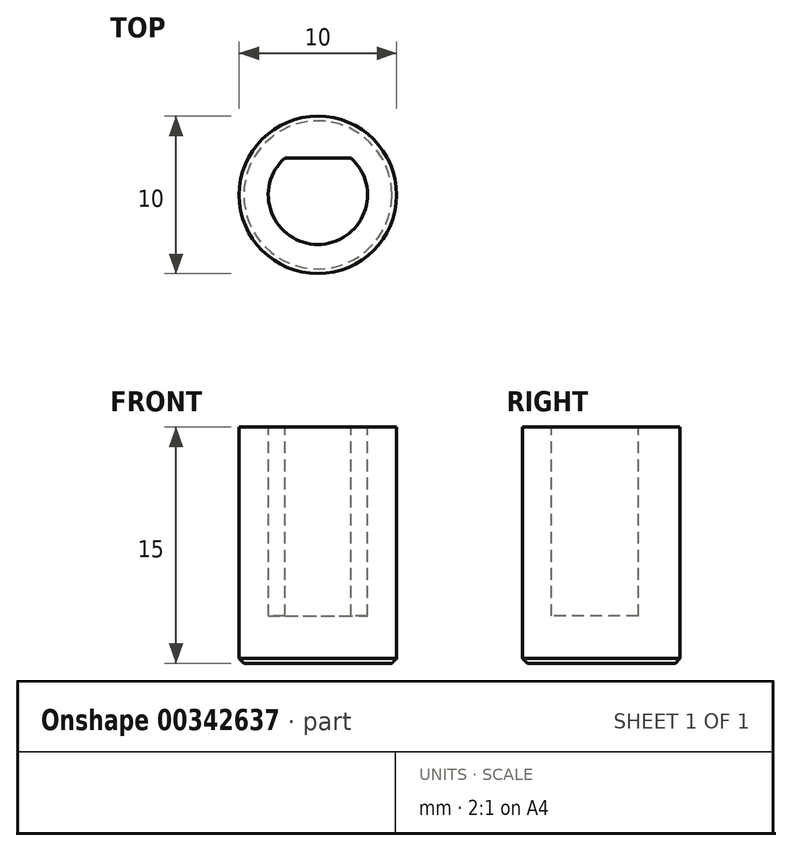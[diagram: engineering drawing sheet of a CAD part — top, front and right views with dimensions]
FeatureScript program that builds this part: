
annotation { "Feature Type Name" : "Feature", "Feature Type Description" : "" }
export const myFeature = defineFeature(function(context is Context, id is Id, definition is map)
    precondition{}
    {
        {
            var Q0;
            Q0=qCreatedBy(makeId("Top.planeOp"),FACE);
            var sketch = newSketch(context, id + "F0", { "sketchPlane" : qUnion([Q0])});
            skCircle(sketch, "E0", {"center": v(0, 0) * mm, "radius": 5 * mm});
            skSolve(sketch);
        }
        {
            var Q0;
            Q0 = qSketchRegion(id + "F0", true);
            extrude(context, id + "F1", {"entities" : qUnion([Q0]), "depth" : 15 * mm});
        }
        {
            var Q0;
            Q0=makeQuery(id+"F1.opExtrude","CAP_FACE",FACE,{"disambiguationData":[OSD([sQuery(id+"F0.wireOp",EDGE,"E0")])],"isStart":false});
            var sketch = newSketch(context, id + "F2", { "sketchPlane" : qUnion([Q0])});
            skArc(sketch, "E1", {"start": v(-2.1, 2.35) * mm, "mid": v(0, -3.15) * mm, "end": v(2.1, 2.35) * mm});
            skLineSegment(sketch, "E2", {"start": v(-2.1, 2.35) * mm, "end": v(2.1, 2.35) * mm});
            skSolve(sketch);
        }
        {
            var Q0;
            Q0 = qSketchRegion(id + "F2", true);
            extrude(context, id + "F3", {"entities" : qUnion([Q0]), "operationType" : NewBodyOperationType.REMOVE, "oppositeDirection" : true, "depth" : 12 * mm});
        }
        {
            var Q0;
            Q0=makeQuery(id+"F1.opExtrude","CAP_FACE",FACE,{"disambiguationData":[OSD([sQuery(id+"F0.wireOp",EDGE,"E0")])],"isStart":true});
            chamfer(context, id + "F4", {"entities" : qUnion([Q0]), "width" : 0.3 * mm, "tangentPropagation" : true});
        }
    });
